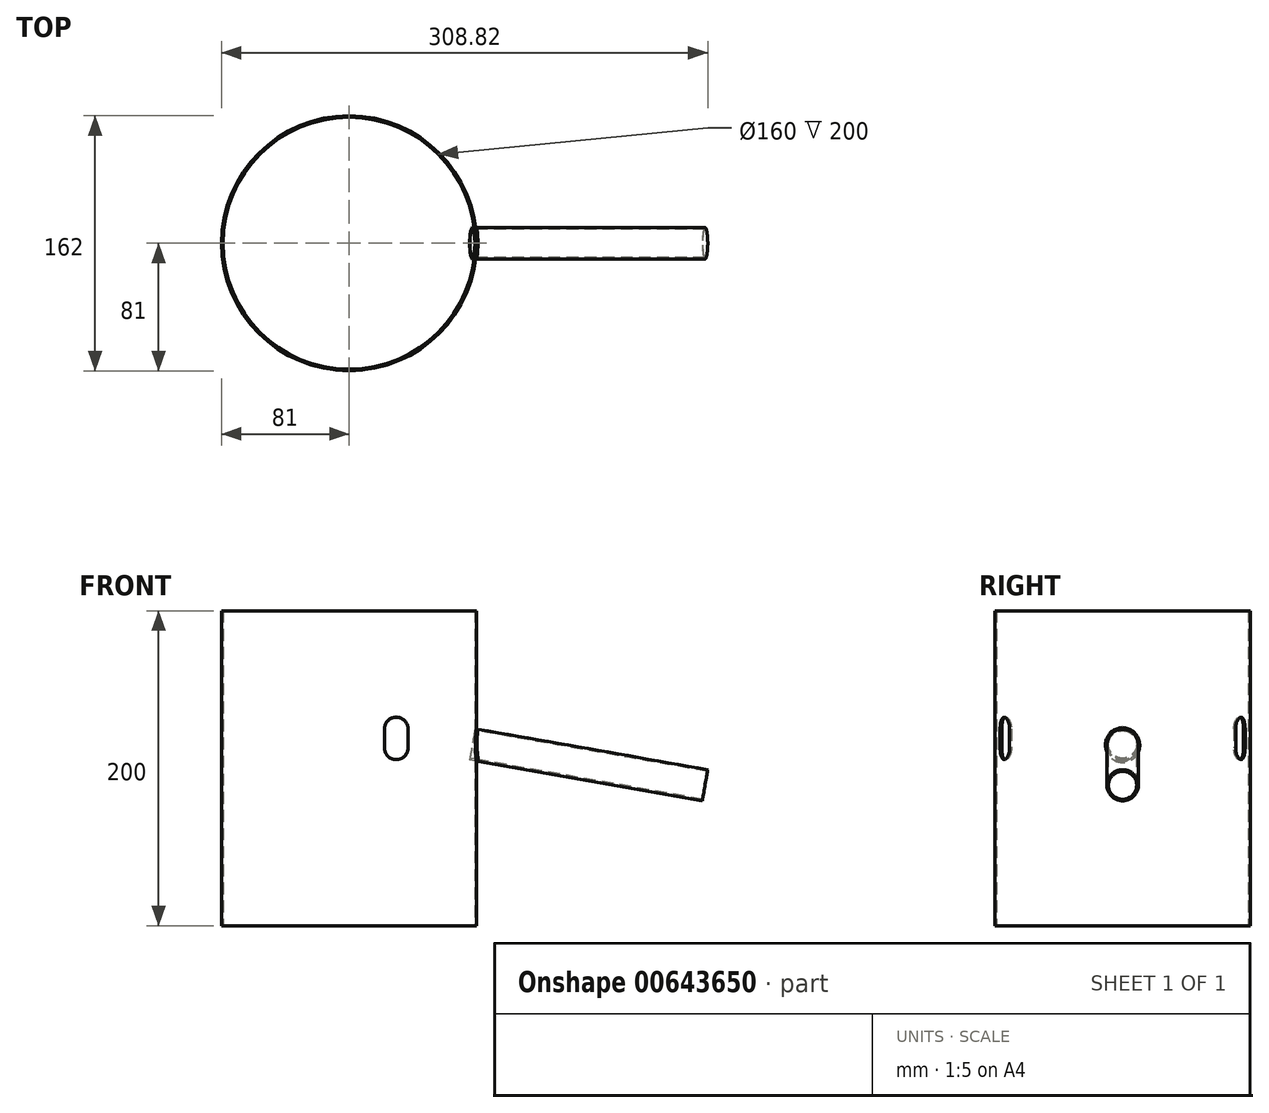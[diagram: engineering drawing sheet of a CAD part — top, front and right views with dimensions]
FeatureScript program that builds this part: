
annotation { "Feature Type Name" : "Feature", "Feature Type Description" : "" }
export const myFeature = defineFeature(function(context is Context, id is Id, definition is map)
    precondition{}
    {
        {
            var Q0;
            Q0=qCreatedBy(makeId("Top.planeOp"),FACE);
            var sketch = newSketch(context, id + "F0", { "sketchPlane" : qUnion([Q0])});
            skCircle(sketch, "E0", {"center": v(0, 0) * mm, "radius": 81 * mm});
            skCircle(sketch, "E1", {"center": v(0, 0) * mm, "radius": 80 * mm});
            skSolve(sketch);
        }
        {
            var Q0;
            Q0 = qSketchRegion(id + "F0", true);
            extrude(context, id + "F1", {"entities" : qUnion([Q0]), "depth" : 200 * mm, "offsetDistance" : 25 * mm});
        }
        {
            var Q0;
            Q0=qCreatedBy(makeId("Front.planeOp"),FACE);
            var sketch = newSketch(context, id + "F2", { "sketchPlane" : qUnion([Q0])});
            skArc(sketch, "E2", {"start": v(37.5, 125) * mm, "mid": v(30, 132.5) * mm, "end": v(22.5, 125) * mm});
            skArc(sketch, "E3", {"start": v(22.5, 113) * mm, "mid": v(30, 105.5) * mm, "end": v(37.5, 113) * mm});
            skLineSegment(sketch, "E4", {"start": v(37.5, 125) * mm, "end": v(37.5, 113) * mm});
            skLineSegment(sketch, "E5", {"start": v(22.5, 125) * mm, "end": v(22.5, 113) * mm});
            skSolve(sketch);
        }
        {
            var Q0;
            Q0 = qSketchRegion(id + "F2", true);
            extrude(context, id + "F3", {"entities" : qUnion([Q0]), "operationType" : NewBodyOperationType.REMOVE, "oppositeDirection" : true, "depth" : 300 * mm, "offsetDistance" : 25 * mm, "symmetric" : true});
        }
        {
            var Q0;
            Q0=qCreatedBy(makeId("Front.planeOp"),FACE);
            var sketch = newSketch(context, id + "F4", { "sketchPlane" : qUnion([Q0])});
            skLineSegment(sketch, "E6", {"start": v(80, 115) * mm, "end": v(236.04, 87.49) * mm, "construction": true});
            skLineSegment(sketch, "E7", {"start": v(80.1, 125.14) * mm, "end": v(79.93, 124.15) * mm});
            skLineSegment(sketch, "E8", {"start": v(79.93, 124.15) * mm, "end": v(227.65, 98.1) * mm});
            skLineSegment(sketch, "E9", {"start": v(227.65, 98.1) * mm, "end": v(227.82, 99.09) * mm});
            skLineSegment(sketch, "E10", {"start": v(227.82, 99.09) * mm, "end": v(80.1, 125.14) * mm});
            skSolve(sketch);
        }
        {
            var Q0;
            Q0 = qSketchRegion(id + "F4", true);
            var Q1;
            Q1=sQuery(id+"F4.wireOp",EDGE,"E6");
            revolve(context, id + "F5", {"operationType" : NewBodyOperationType.ADD, "entities" : qUnion([Q0]), "axis" : qUnion([Q1]), "revolveType" : RevolveType.FULL});
        }
        {
            var Q0;
            Q0=makeQuery(id+"F5.boolean.opBoolean","INTERSECT",EDGE,{"derivedFrom":[makeQuery(id+"F1.opExtrude","SWEPT_FACE",FACE,{"disambiguationData":[OSD([sQuery(id+"F0.wireOp",EDGE,"E0")])]}),makeQuery(id+"F5.opRevolve","SWEPT_FACE",FACE,{"disambiguationData":[OSD([sQuery(id+"F4.wireOp",EDGE,"E10")])]})]});
            fillet(context, id + "F6", {"entities" : qUnion([Q0]), "radius" : 1 * mm, "tangentPropagation" : true, "allowEdgeOverflow" : false});
        }
    });
